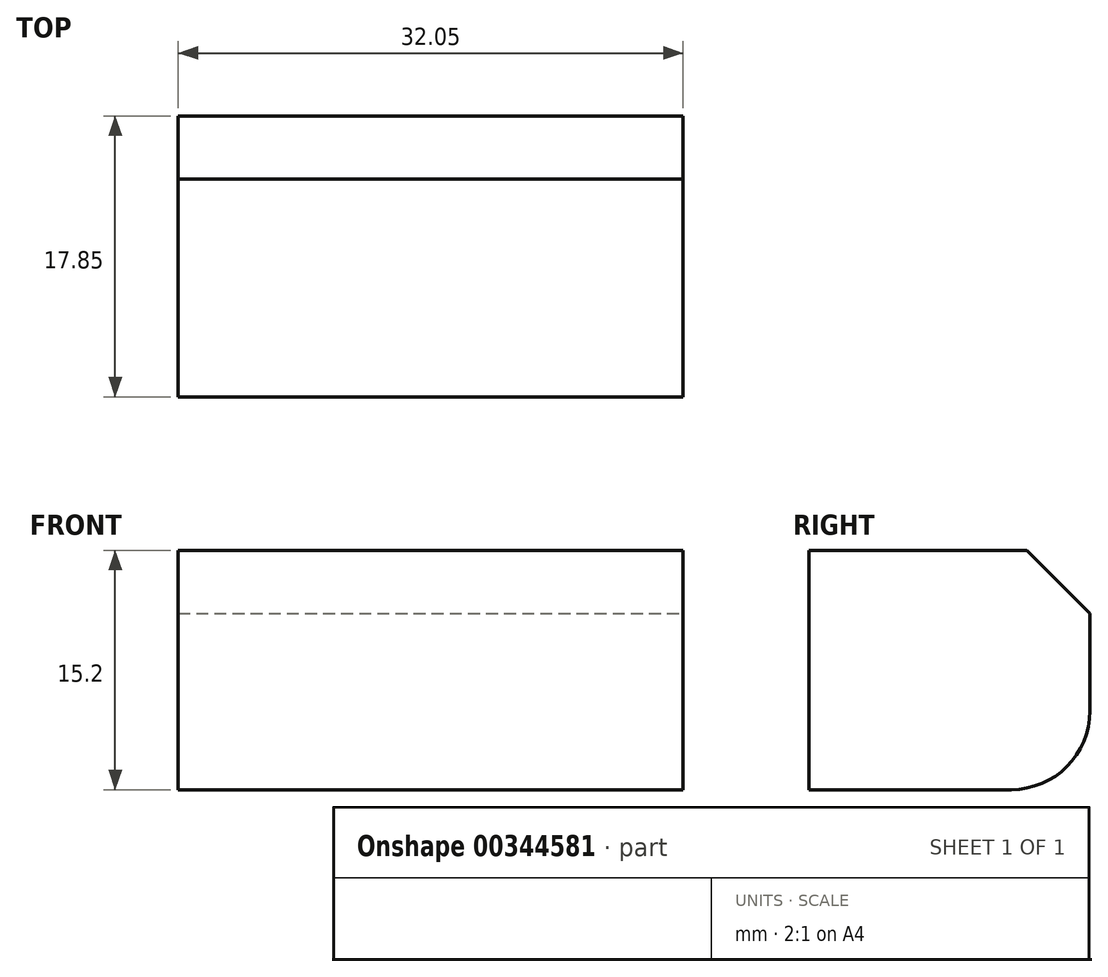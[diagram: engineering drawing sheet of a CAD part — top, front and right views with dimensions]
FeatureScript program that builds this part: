
annotation { "Feature Type Name" : "Feature", "Feature Type Description" : "" }
export const myFeature = defineFeature(function(context is Context, id is Id, definition is map)
    precondition{}
    {
        {
            var Q0;
            Q0=qCreatedBy(makeId("Top.planeOp"),FACE);
            var sketch = newSketch(context, id + "F0", { "sketchPlane" : qUnion([Q0])});
            skLineSegment(sketch, "E0.bottom", {"start": v(0, 0) * mm, "end": v(32.05, 0) * mm});
            skLineSegment(sketch, "E0.top", {"start": v(0, -17.85) * mm, "end": v(32.05, -17.85) * mm});
            skLineSegment(sketch, "E0.left", {"start": v(0, 0) * mm, "end": v(0, -17.85) * mm});
            skLineSegment(sketch, "E0.right", {"start": v(32.05, 0) * mm, "end": v(32.05, -17.85) * mm});
            skSolve(sketch);
        }
        {
            var Q0;
            Q0=makeQuery(id+"F0.imprint","IMPRINT",FACE,{"disambiguationData":[TD([[makeQuery(id+"F0.imprint","IMPRINT",EDGE,{"derivedFrom":sQuery(id+"F0.wireOp",EDGE,"E0.bottom")}),-1.0]])]});
            extrude(context, id + "F1", {"entities" : qUnion([Q0]), "depth" : 15.2 * mm});
        }
        {
            var Q0;
            Q0=makeQuery(id+"F1.opExtrude","CAP_EDGE",EDGE,{"disambiguationData":[OSD([sQuery(id+"F0.wireOp",EDGE,"E0.bottom")])],"isStart":false});
            chamfer(context, id + "F2", {"entities" : qUnion([Q0]), "width" : 4 * mm, "tangentPropagation" : true});
        }
        {
            var Q0;
            Q0=makeQuery(id+"F1.opExtrude","CAP_EDGE",EDGE,{"disambiguationData":[OSD([sQuery(id+"F0.wireOp",EDGE,"E0.bottom")])],"isStart":true});
            fillet(context, id + "F3", {"entities" : qUnion([Q0]), "radius" : 5 * mm, "tangentPropagation" : true, "allowEdgeOverflow" : false});
        }
    });
